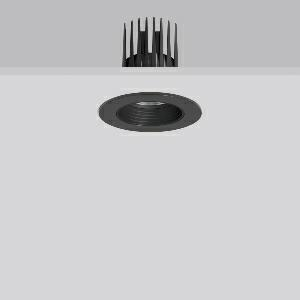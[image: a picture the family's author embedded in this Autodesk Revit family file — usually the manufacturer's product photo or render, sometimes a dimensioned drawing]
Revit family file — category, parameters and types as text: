
# Revit family: heledon_mini_e_901754_003_1_76_5884
name_source: partatom
category: Lighting Fixtures
units: mm (PartAtom-declared; Revit-internal decimal feet)

## family parameters
Cut with Voids When Loaded = No
Host = Face
Light Source = No
Part Type = Normal
Room Calculation Point = No
Round Connector Dimension = Use Diameter
Shared = No

## types (1)
- HELEDON mini E (1 x LED Modul 940, 3500 lm, 4000)
    Apparent Load = 29 VA
    Approval mark = CE
    CIE Flux Codes = 80 99 100 100 100
    Color Rendering = 92
    Color Temperature = 4000
    Default Elevation = 1800 mm
    Description = Series: HELEDON mini
Round recessed downlight. Housing: die-cast aluminium, powder-coated. Black plastic ring and recessed LED to prevent glare from the side. Optical assembly with lens made of plastic (polycarbonate) for the best homogeneous light distribution - can be changed without tools. Best colour rendering index Ra>90. Suitable for Recessed ceiling mounting. Installation without tools thanks to spring fastening system. Including separate LED converter with connecting cable 600 mm.High quality converter without flickering and stroboscopic effect. Through-wiring box (5 pole) available as accessory. The following accessories can be mounted without use of tools: interchangeable lenses, decorative glasses, honeycomb louvre, clear and frosted diffusers, white interchangeable plastic ring. 
Colour: deep black, matt (RAL 9005)
Diameter: 124 mm
Height: 3 mm
Cut-out diameter: 114 mm
Recess height: 170 mm
Luminaire: recess height: 120 mm
Lamp: LED
Socket: without socket
Colour temperature: 4000K
Colour rendering index (CRI): 92
System power: 29 W
Rated luminous flux: 3500 lm
Luminous efficiency: 121 lm/W
Control gear: Converter, dimmable, DALI
Protection class: II
Type of protection: IP 20
    Height = 0 mm  [stored 0 ft]
    Lamp = 1 x LED Modul 940
    Lamp Light Flux = 3500 lm
    Lamp count = 1
    Length = 124 mm  [stored 0.406824 ft]
    Lifetime = 50000 h
    Luminous efficacy = 121 lm/W
    Manufacturer = RZB
    ModVariant = No
    Model = 901754.003.1.76
    Mounting Place = Ceiling
    Mounting Type = Recessed
    Number of Poles = 1
    OnlyDefault = Yes
    Power Factor = 1
    Product Name = HELEDON mini E
    Product group = Recessed downlights
    ProductGroupID = 402
    Protection Class = Protection class II
    Protection Degree = IP 20
    RLX_Detail_Level = 1
    RLX_Emergency_Light_Flux = 0 lm
    RLX_Emergency_Type = 0
    RLX_Emergency_Type_DB = No
    RlxData = <blob elided: 125373 chars, md5=82f80a0a>
    Socket = socket
    Standby Power = 0 W
    System Light Flux = 3500 lm
    System Power = 29 W
    Type Comments = Product without accessories
    Type Image = 901656.003.jpg
    URL = http://relux.com
    VarID = ---
    Voltage = 230 V
    Voltage Range = 220-240 V
    Weight = 0.00 kg
    Width = 0 mm  [stored 0 ft]

note: [stored X ft] marks values corroborated as IEEE doubles in the binary element streams (Revit-internal decimal feet)

## geometry (parser evidence)
native form markers: Blend x4, Sweep x11
no freeform markers — native parametric forms only
